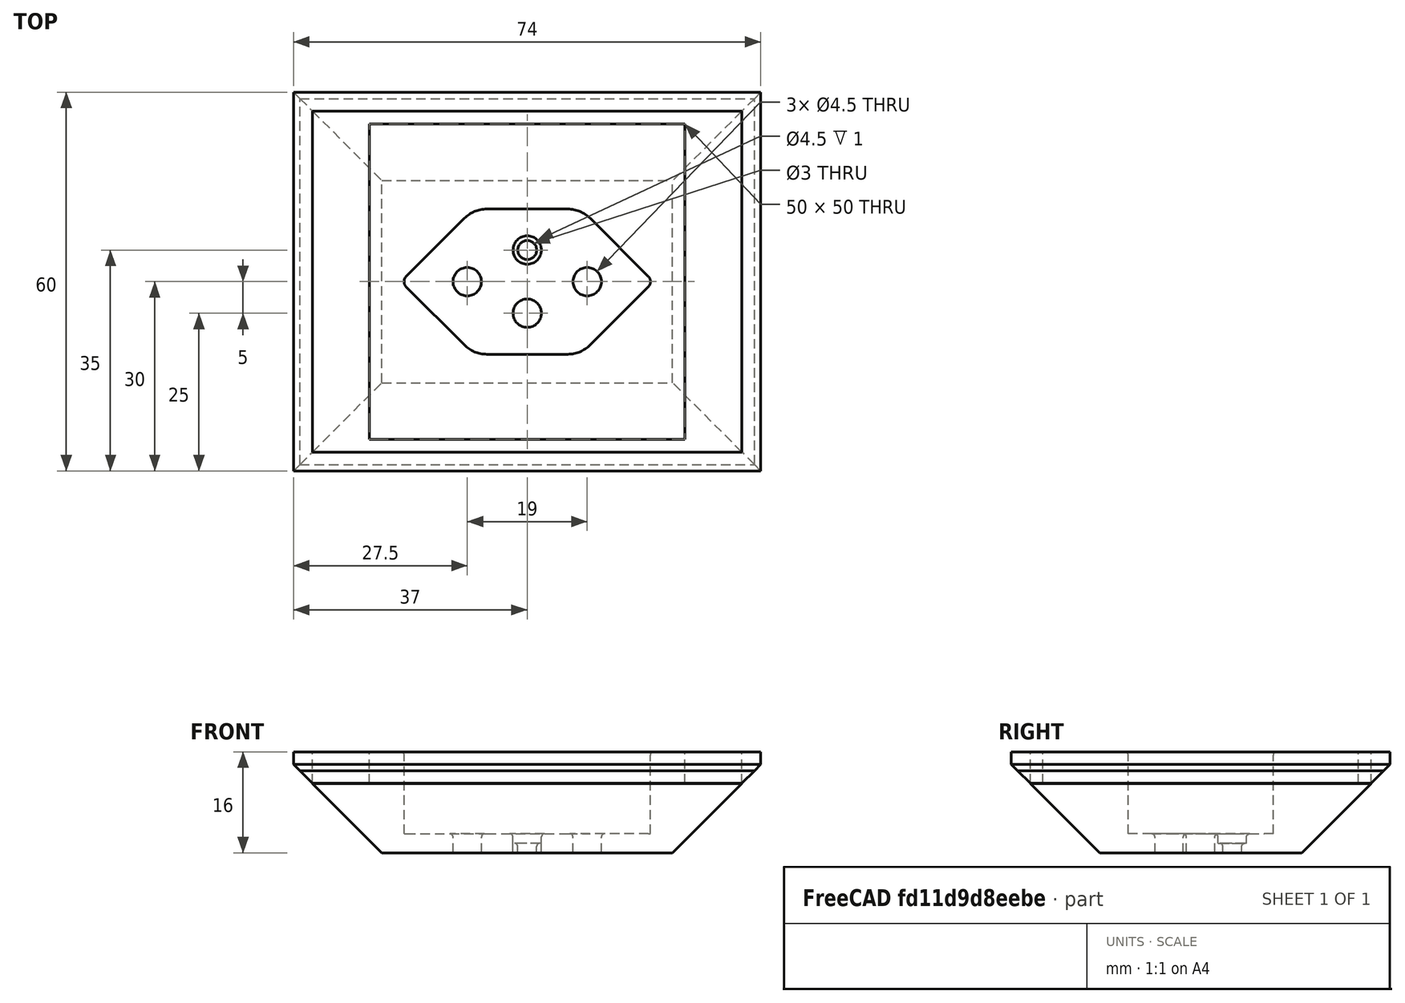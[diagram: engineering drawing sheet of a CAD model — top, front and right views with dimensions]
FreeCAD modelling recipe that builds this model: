
FCSTD DOCUMENT  (FreeCAD 0.16R)
Label: Steckdose_230V_CH_einfach_basis
License: All rights reserved
LicenseURL: http://en.wikipedia.org/wiki/All_rights_reserved
objects: Part::Cut×11, Part::Box×9, Part::Cylinder×5, Part::Chamfer×5, Part::Fillet×4, Part::Fuse×1
note: 35 computed .brp shape members not serialized (recipe doc carries the construction recipe); baked Part::Feature solids carry a one-line shape summary decoded from their .brp

FEATURE [Part::Box] Box  label="Basis"
  Height = 19
  Length = 68
  Placement = pos=(-34,-27,0) rot=(0,0,1;0rad)
  Width = 54
FEATURE [Part::Cylinder] Cylinder  label="Cylinder000"
  Angle = 360
  Height = 20
  Placement = pos=(-9.5,0,0) rot=(0,0,1;0rad)
  Radius = 2.25
FEATURE [Part::Cylinder] Cylinder001
  Angle = 360
  Height = 20
  Placement = pos=(9.5,0,0) rot=(0,0,1;0rad)
  Radius = 2.25
FEATURE [Part::Cylinder] Cylinder002
  Angle = 360
  Height = 20
  Placement = pos=(0,-5,0) rot=(0,0,1;0rad)
  Radius = 2.25
FEATURE [Part::Cylinder] Cylinder003
  Angle = 360
  Height = 20
  Placement = pos=(0,5,1.5) rot=(0,0,1;0rad)
  Radius = 2.25
FEATURE [Part::Cylinder] Cylinder004
  Angle = 360
  Height = 20
  Placement = pos=(0,5,0) rot=(0,0,1;0rad)
  Radius = 1.5
FEATURE [Part::Box] Box001  label="Cube001"
  Height = 16
  Length = 39
  Placement = pos=(50,0,0) rot=(0,0,1;0rad)
  Width = 23
FEATURE [Part::Chamfer] Chamfer
  Base = -> Box001
  Edges = 4 edges r=11: [Edge1,Edge3,Edge5,Edge7]
FEATURE [Part::Fillet] Fillet
  Base = -> Chamfer
  Edges = 4 edges r=1: [Edge2,Edge3,Edge23,Edge24]
FEATURE [Part::Fillet] Fillet001  label="Ausschnitt"
  Base = -> Fillet
  Edges = 4 edges r=5: [Edge29,Edge30,Edge31,Edge32]
  Placement = pos=(-69.5,-11.5,3) rot=(0,0,1;0rad)
FEATURE [Part::Cut] Cut
  Base = -> Box
  Tool = -> Fillet001
FEATURE [Part::Cut] Cut001
  Base = -> Cut
  Tool = -> Cylinder
FEATURE [Part::Cut] Cut002
  Base = -> Cut001
  Tool = -> Cylinder001
FEATURE [Part::Cut] Cut003
  Base = -> Cut002
  Tool = -> Cylinder002
FEATURE [Part::Cut] Cut004
  Base = -> Cut003
  Tool = -> Cylinder003
FEATURE [Part::Cut] Cut005
  Base = -> Cut004
  Placement = pos=(37,-30,28) rot=(0,0,1;0rad)
  Tool = -> Cylinder004
FEATURE [Part::Box] Box032  label="Basis Stecker"
  Height = 42
  Length = 74
  Placement = pos=(0,-60,0) rot=(0,0,1;0rad)
  Width = 60
FEATURE [Part::Box] Box033  label="Ausschnitt Stecker"
  Height = 42
  Length = 72
  Placement = pos=(1,-59,0) rot=(0,0,1;0rad)
  Width = 58
FEATURE [Part::Cut] Cut014
  Base = -> Box032
  Tool = -> Box033
FEATURE [Part::Chamfer] Chamfer020
  Base = -> Cut014
  Edges = 4 edges r=0.99: [Edge10,Edge11,Edge12,Edge13]
FEATURE [Part::Box] Box038  label="Kragen Stecker"
  Height = 4.1
  Length = 74
  Placement = pos=(0,-60,0) rot=(0,0,1;0rad)
  Width = 60
FEATURE [Part::Box] Box039  label="Kragen Stecker Ausschnitt"
  Height = 4.1
  Length = 68
  Placement = pos=(3,-57,0) rot=(0,0,1;0rad)
  Width = 54
FEATURE [Part::Cut] Cut019
  Base = -> Box038
  Placement = pos=(0,0,36.9) rot=(0,0,1;0rad)
  Tool = -> Box039
FEATURE [Part::Chamfer] Chamfer021
  Base = -> Cut019
  Edges = 4 edges r=2: [Edge10,Edge11,Edge12,Edge13]
FEATURE [Part::Chamfer] Chamfer022
  Base = -> Chamfer021
  Edges = 4 edges r=2: [Edge26,Edge29,Edge31,Edge32]
FEATURE [Part::Fuse] Fusion  label="Form"
  Base = -> Chamfer020
  Tool = -> Chamfer022
FEATURE [Part::Box] Box040  label="Cube"
  Height = 10
  Length = 74
  Placement = pos=(0,-60,44) rot=(0,0,1;0rad)
  Width = 60
FEATURE [Part::Box] Box041  label="Cube002"
  Height = 5
  Length = 74
  Placement = pos=(0,-60,39) rot=(0,0,1;0rad)
  Width = 60
FEATURE [Part::Box] Box042  label="Cube003"
  Height = 13
  Length = 50
  Placement = pos=(12,-55,32) rot=(0,0,1;0rad)
  Width = 50
FEATURE [Part::Cut] Cut020
  Base = -> Cut005
  Tool = -> Box040
FEATURE [Part::Cut] Cut021
  Base = -> Box041
  Tool = -> Fusion
FEATURE [Part::Cut] Cut022
  Base = -> Cut021
  Tool = -> Box042
FEATURE [Part::Chamfer] Chamfer023
  Base = -> Cut020
  Edges = 4 edges r=10.99: [Edge4,Edge7,Edge27,Edge28]
FEATURE [Part::Fillet] Fillet002
  Base = -> Chamfer023
  Edges = 16 edges r=0.5: [Edge13,Edge14,Edge15,Edge16,Edge17,Edge18,Edge19,Edge20,Edge21,Edge22,Edge23,Edge24,Edge25,Edge26,Edge27,Edge28]
FEATURE [Part::Fillet] Fillet003
  Base = -> Fillet002
  Edges = 5 edges r=0.5: [Edge101,Edge102,Edge103,Edge104,Edge114]
